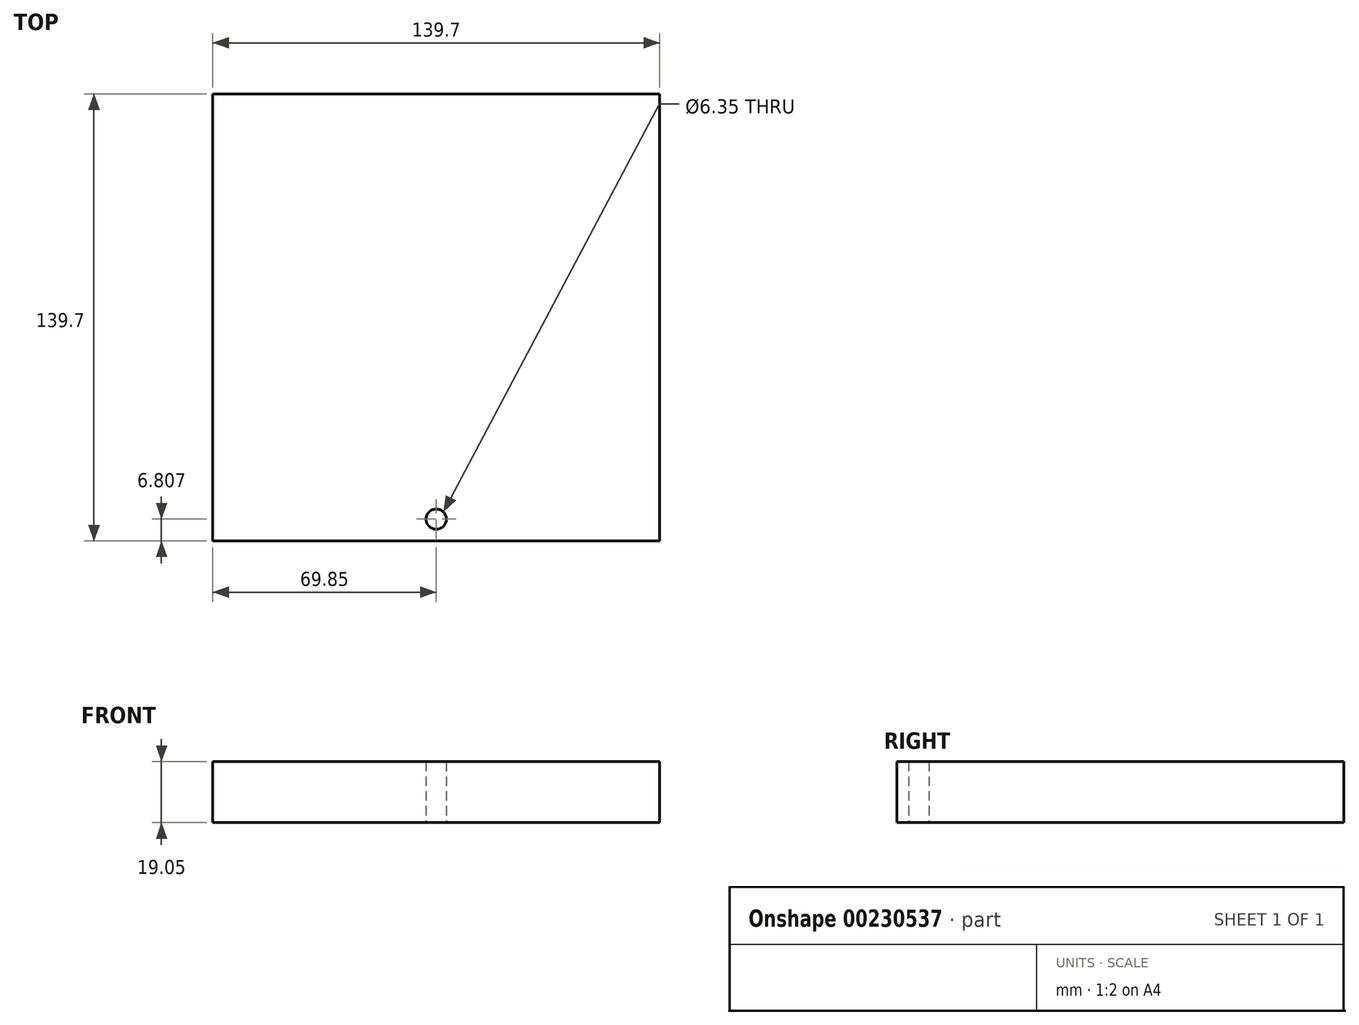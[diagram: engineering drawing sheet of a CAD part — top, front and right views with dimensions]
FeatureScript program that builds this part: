
annotation { "Feature Type Name" : "Feature", "Feature Type Description" : "" }
export const myFeature = defineFeature(function(context is Context, id is Id, definition is map)
    precondition{}
    {
        {
            var Q0;
            Q0=qCreatedBy(makeId("Top.planeOp"),FACE);
            var sketch = newSketch(context, id + "F0", { "sketchPlane" : qUnion([Q0])});
            skLineSegment(sketch, "E0", {"start": v(0, -75.74) * mm, "end": v(0, -63.04) * mm});
            skCircle(sketch, "E1", {"center": v(0, -63.04) * mm, "radius": 3.18 * mm});
            skLineSegment(sketch, "E2.bottom", {"start": v(69.85, -69.85) * mm, "end": v(-69.85, -69.85) * mm});
            skLineSegment(sketch, "E2.top", {"start": v(69.85, 69.85) * mm, "end": v(-69.85, 69.85) * mm});
            skLineSegment(sketch, "E2.left", {"start": v(69.85, -69.85) * mm, "end": v(69.85, 69.85) * mm});
            skLineSegment(sketch, "E2.right", {"start": v(-69.85, -69.85) * mm, "end": v(-69.85, 69.85) * mm});
            skPoint(sketch, "E2.middle", {"position": v(0, 0) * mm});
            skSolve(sketch);
        }
        {
            var Q0;
            Q0 = qSketchRegion(id + "F0", true);
            extrude(context, id + "F1", {"entities" : qUnion([Q0]), "depth" : 19.05 * mm});
        }
    });
